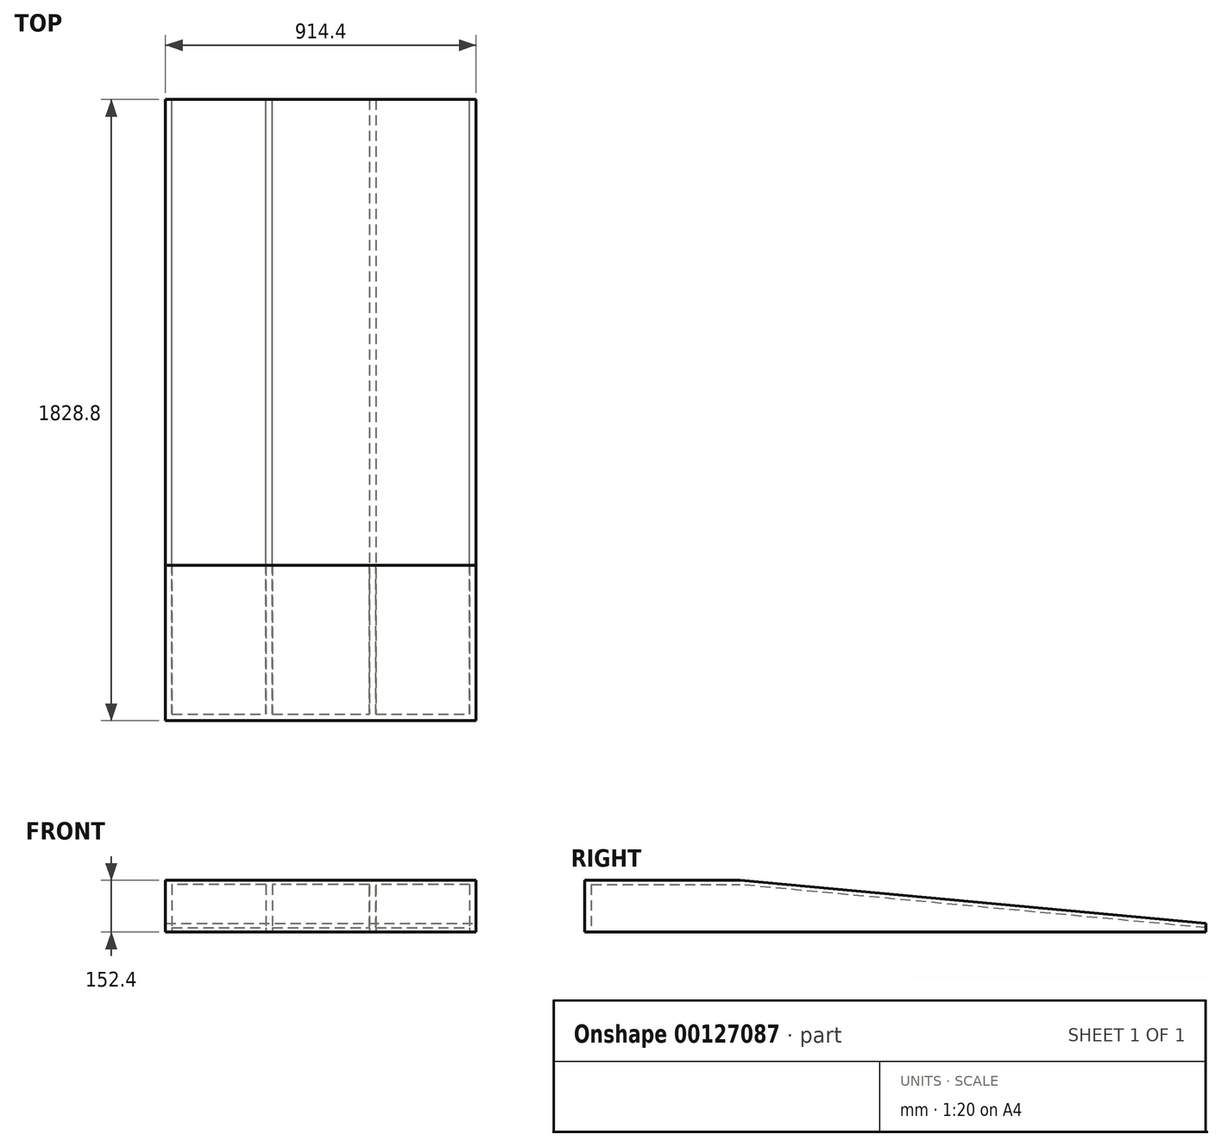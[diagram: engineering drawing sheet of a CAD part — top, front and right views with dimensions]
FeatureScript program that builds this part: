
annotation { "Feature Type Name" : "Feature", "Feature Type Description" : "" }
export const myFeature = defineFeature(function(context is Context, id is Id, definition is map)
    precondition{}
    {
        {
            var Q0;
            Q0=qCreatedBy(makeId("Right.planeOp"),FACE);
            var sketch = newSketch(context, id + "F0", { "sketchPlane" : qUnion([Q0])});
            skLineSegment(sketch, "E0.bottom", {"start": v(0, 0) * mm, "end": v(1828.8, 0) * mm});
            skLineSegment(sketch, "E0.top", {"start": v(0, 152.4) * mm, "end": v(457.2, 152.4) * mm});
            skLineSegment(sketch, "E0.left", {"start": v(0, 0) * mm, "end": v(0, 152.4) * mm});
            skLineSegment(sketch, "E0.right", {"start": v(1828.8, 0) * mm, "end": v(1828.8, 25.4) * mm});
            skLineSegment(sketch, "E1", {"start": v(1828.8, 25.4) * mm, "end": v(457.2, 152.4) * mm});
            skSolve(sketch);
        }
        {
            var Q0;
            Q0 = qSketchRegion(id + "F0", true);
            extrude(context, id + "F1", {"entities" : qUnion([Q0]), "oppositeDirection" : true, "depth" : 914.4 * mm, "offsetDistance" : 30.48 * mm});
        }
        {
            var Q0;
            Q0=makeQuery(id+"F1.opExtrude","SWEPT_FACE",FACE,{"disambiguationData":[OSD([sQuery(id+"F0.wireOp",EDGE,"E0.bottom")])]});
            var sketch = newSketch(context, id + "F2", { "sketchPlane" : qUnion([Q0])});
            skLineSegment(sketch, "E2.0", {"start": v(-19.05, -19.05) * mm, "end": v(-19.05, -1828.8) * mm});
            skLineSegment(sketch, "E2.1", {"start": v(-895.35, -19.05) * mm, "end": v(-619.13, -19.05) * mm});
            skLineSegment(sketch, "E2.2", {"start": v(-895.35, -19.05) * mm, "end": v(-895.35, -1828.8) * mm});
            skLineSegment(sketch, "E3", {"start": v(-19.05, -1828.8) * mm, "end": v(-895.35, -1828.8) * mm, "construction": true});
            skLineSegment(sketch, "E4", {"start": v(-609.6, -19.05) * mm, "end": v(-609.6, -1828.8) * mm, "construction": true});
            skLineSegment(sketch, "E5", {"start": v(-304.8, -1828.8) * mm, "end": v(-304.8, -19.05) * mm, "construction": true});
            skLineSegment(sketch, "E6.0", {"start": v(-295.27, -1828.8) * mm, "end": v(-295.28, -19.05) * mm});
            skLineSegment(sketch, "E7.0", {"start": v(-619.13, -19.05) * mm, "end": v(-619.13, -1828.8) * mm});
            skLineSegment(sketch, "E8.0", {"start": v(-600.08, -19.05) * mm, "end": v(-600.08, -1828.8) * mm});
            skLineSegment(sketch, "E9.0", {"start": v(-314.32, -1828.8) * mm, "end": v(-314.33, -19.05) * mm});
            skLineSegment(sketch, "E10.trimOffspring", {"start": v(-600.08, -19.05) * mm, "end": v(-314.33, -19.05) * mm});
            skLineSegment(sketch, "E11.trimOffspring", {"start": v(-295.28, -19.05) * mm, "end": v(-19.05, -19.05) * mm});
            skSolve(sketch);
        }
        {
            var Q0;
            {var subQ0=sQuery(id+"F2.wireOp",EDGE,"E2.2");Q0=makeQuery(id+"F2.imprint","IMPRINT",FACE,{"disambiguationData":[TD([[makeQuery(id+"F2.imprint","IMPRINT",EDGE,{"derivedFrom":subQ0}),1.0]])]});}
            var Q1;
            {var subQ0=sQuery(id+"F2.wireOp",EDGE,"E2.0");Q1=makeQuery(id+"F2.imprint","IMPRINT",FACE,{"disambiguationData":[TD([[makeQuery(id+"F2.imprint","IMPRINT",EDGE,{"derivedFrom":subQ0}),-1.0]])]});}
            var Q2;
            {var subQ0=sQuery(id+"F2.wireOp",EDGE,"E8.0");Q2=makeQuery(id+"F2.imprint","IMPRINT",FACE,{"disambiguationData":[TD([[makeQuery(id+"F2.imprint","IMPRINT",EDGE,{"derivedFrom":subQ0}),1.0]])]});}
            extrude(context, id + "F3", {"entities" : qUnion([Q0, Q1, Q2]), "operationType" : NewBodyOperationType.REMOVE, "endBound" : BoundingType.UP_TO_NEXT, "oppositeDirection" : true, "depth" : 344.77 * mm, "hasOffset" : true, "offsetDistance" : 12.7 * mm});
        }
    });
